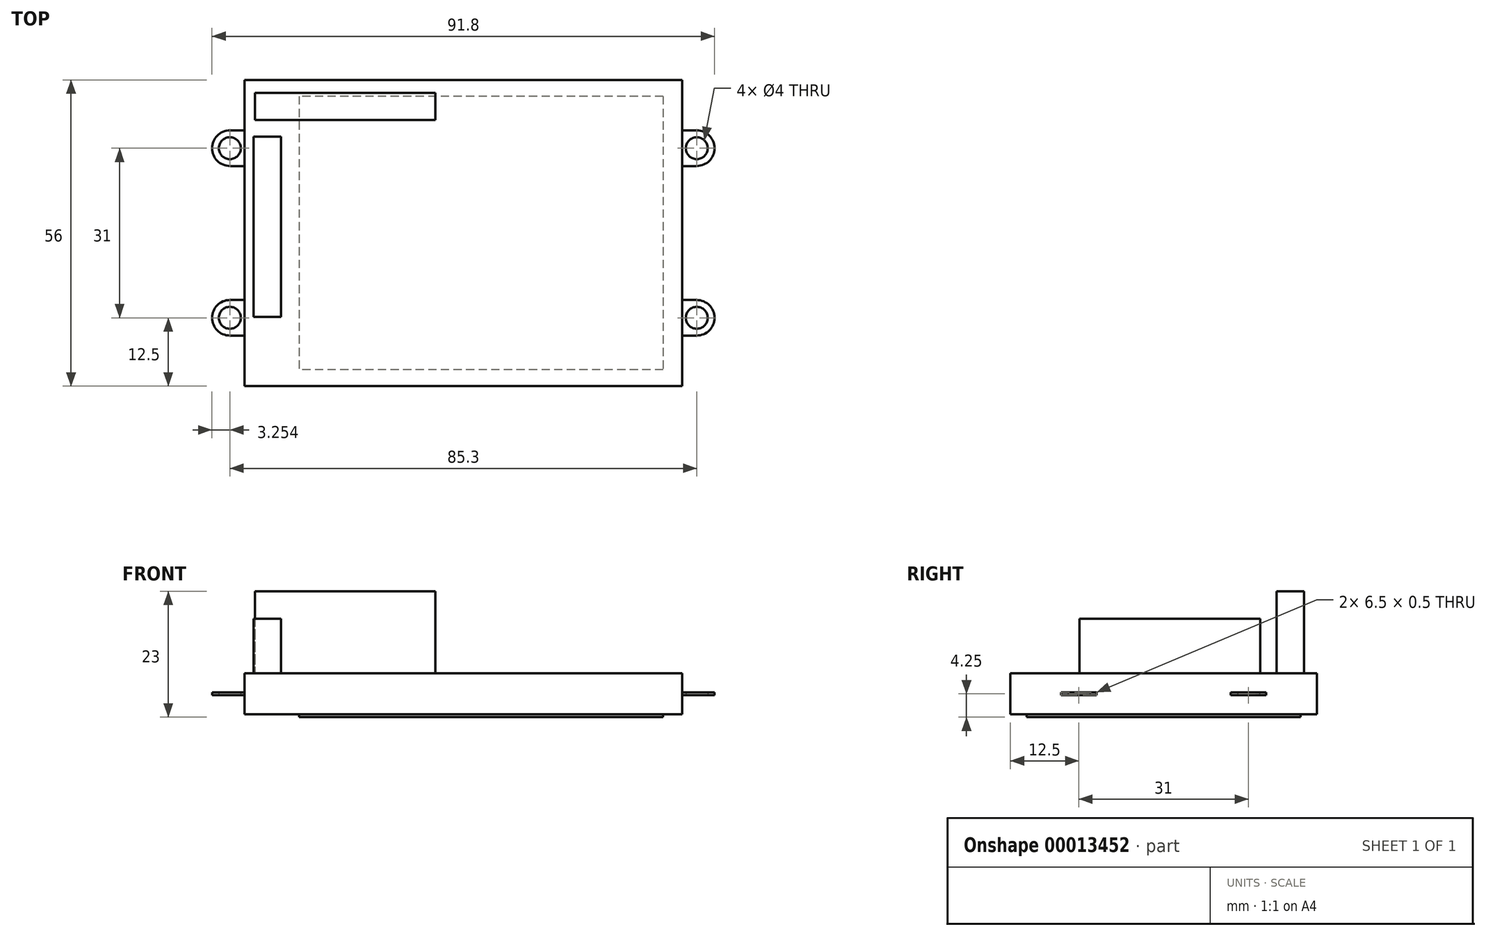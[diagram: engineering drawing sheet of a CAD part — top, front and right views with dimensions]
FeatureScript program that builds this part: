
annotation { "Feature Type Name" : "Feature", "Feature Type Description" : "" }
export const myFeature = defineFeature(function(context is Context, id is Id, definition is map)
    precondition{}
    {
        {
            var Q0;
            Q0=qCreatedBy(makeId("Top.planeOp"),FACE);
            var sketch = newSketch(context, id + "F0", { "sketchPlane" : qUnion([Q0])});
            skLineSegment(sketch, "E0.bottom", {"start": v(-42.56, 23.8) * mm, "end": v(37.44, 23.8) * mm});
            skLineSegment(sketch, "E0.top", {"start": v(-42.56, -32.2) * mm, "end": v(37.44, -32.2) * mm});
            skLineSegment(sketch, "E0.left", {"start": v(-42.56, 23.8) * mm, "end": v(-42.56, -16.44) * mm});
            skLineSegment(sketch, "E0.right", {"start": v(37.44, 23.8) * mm, "end": v(37.44, -32.2) * mm});
            skLineSegment(sketch, "E1", {"start": v(37.44, -22.94) * mm, "end": v(40.1, -22.94) * mm, "construction": true});
            skLineSegment(sketch, "E2", {"start": v(37.44, -16.44) * mm, "end": v(40.1, -16.44) * mm, "construction": true});
            skArc(sketch, "E3", {"start": v(40.1, -22.94) * mm, "mid": v(43.34, -19.7) * mm, "end": v(40.1, -16.44) * mm});
            skCircle(sketch, "E4", {"center": v(40.1, -19.7) * mm, "radius": 2 * mm});
            skLineSegment(sketch, "E5", {"start": v(40.1, -16.44) * mm, "end": v(40.1, -22.94) * mm, "construction": true});
            skLineSegment(sketch, "E6", {"start": v(-2.56, 23.8) * mm, "end": v(-2.56, -32.2) * mm, "construction": true});
            skLineSegment(sketch, "E7", {"start": v(-42.56, -4.2) * mm, "end": v(37.44, -4.2) * mm, "construction": true});
            skLineSegment(sketch, "E8.0.MirrorCS", {"start": v(-45.2, -16.44) * mm, "end": v(-45.2, -22.94) * mm, "construction": true});
            skCircle(sketch, "E8.1.MirrorC", {"center": v(-45.2, -19.7) * mm, "radius": 2 * mm});
            skLineSegment(sketch, "E8.2.MirrorCS", {"start": v(-42.56, -22.94) * mm, "end": v(-45.2, -22.94) * mm, "construction": true});
            skLineSegment(sketch, "E8.3.MirrorCS", {"start": v(-42.56, -16.44) * mm, "end": v(-45.2, -16.44) * mm, "construction": true});
            skArc(sketch, "E8.4.MirrorCS", {"start": v(-45.2, -22.94) * mm, "mid": v(-48.46, -19.7) * mm, "end": v(-45.2, -16.44) * mm});
            skLineSegment(sketch, "E9.3.MirrorCS", {"start": v(37.44, -22.94) * mm, "end": v(40.1, -22.94) * mm});
            skLineSegment(sketch, "E10.1.MirrorCS", {"start": v(-42.56, -16.44) * mm, "end": v(-45.2, -16.44) * mm});
            skLineSegment(sketch, "E10.8.MirrorCS", {"start": v(37.44, -16.44) * mm, "end": v(40.1, -16.44) * mm});
            skLineSegment(sketch, "E11.6.MirrorCS", {"start": v(-42.56, -22.94) * mm, "end": v(-45.2, -22.94) * mm});
            skLineSegment(sketch, "E11.9.MirrorCS", {"start": v(-42.56, 23.8) * mm, "end": v(-42.56, -32.2) * mm});
            skArc(sketch, "E12.0.MirrorCS", {"start": v(-45.2, 14.56) * mm, "mid": v(-48.46, 11.3) * mm, "end": v(-45.2, 8.06) * mm});
            skLineSegment(sketch, "E12.1.MirrorCS", {"start": v(-42.56, 14.56) * mm, "end": v(-45.2, 14.56) * mm, "construction": true});
            skLineSegment(sketch, "E12.2.MirrorCS", {"start": v(-45.2, 8.06) * mm, "end": v(-45.2, 14.56) * mm, "construction": true});
            skLineSegment(sketch, "E12.3.MirrorCS", {"start": v(-42.56, 8.06) * mm, "end": v(-45.2, 8.06) * mm, "construction": true});
            skCircle(sketch, "E12.4.MirrorC", {"center": v(-45.2, 11.3) * mm, "radius": 2 * mm});
            skArc(sketch, "E12.5.MirrorCS", {"start": v(-45.2, 14.56) * mm, "mid": v(-48.46, 11.3) * mm, "end": v(-45.2, 8.06) * mm});
            skLineSegment(sketch, "E12.6.MirrorCS", {"start": v(-45.2, 8.06) * mm, "end": v(-45.2, 14.56) * mm, "construction": true});
            skLineSegment(sketch, "E12.7.MirrorCS", {"start": v(-42.56, 8.06) * mm, "end": v(-45.2, 8.06) * mm});
            skLineSegment(sketch, "E12.8.MirrorCS", {"start": v(-42.56, 14.56) * mm, "end": v(-45.2, 14.56) * mm, "construction": true});
            skCircle(sketch, "E12.9.MirrorC", {"center": v(-45.2, 11.3) * mm, "radius": 2 * mm});
            skLineSegment(sketch, "E12.10.MirrorCS", {"start": v(-42.56, 14.56) * mm, "end": v(-45.2, 14.56) * mm, "construction": true});
            skArc(sketch, "E12.11.MirrorCS", {"start": v(-45.2, 14.56) * mm, "mid": v(-48.46, 11.3) * mm, "end": v(-45.2, 8.06) * mm});
            skLineSegment(sketch, "E12.12.MirrorCS", {"start": v(-45.2, 8.06) * mm, "end": v(-45.2, 14.56) * mm, "construction": true});
            skLineSegment(sketch, "E12.13.MirrorCS", {"start": v(-42.56, 8.06) * mm, "end": v(-45.2, 8.06) * mm, "construction": true});
            skLineSegment(sketch, "E12.14.MirrorCS", {"start": v(-42.56, 14.56) * mm, "end": v(-45.2, 14.56) * mm, "construction": true});
            skCircle(sketch, "E12.15.MirrorC", {"center": v(-45.2, 11.3) * mm, "radius": 2 * mm});
            skArc(sketch, "E12.16.MirrorCS", {"start": v(-45.2, 14.56) * mm, "mid": v(-48.46, 11.3) * mm, "end": v(-45.2, 8.06) * mm});
            skLineSegment(sketch, "E12.17.MirrorCS", {"start": v(-45.2, 8.06) * mm, "end": v(-45.2, 14.56) * mm, "construction": true});
            skLineSegment(sketch, "E12.18.MirrorCS", {"start": v(-42.56, 8.06) * mm, "end": v(-45.2, 8.06) * mm, "construction": true});
            skLineSegment(sketch, "E12.19.MirrorCS", {"start": v(-42.56, 14.56) * mm, "end": v(-45.2, 14.56) * mm, "construction": true});
            skLineSegment(sketch, "E12.20.MirrorCS", {"start": v(-42.56, 8.06) * mm, "end": v(-45.2, 8.06) * mm, "construction": true});
            skCircle(sketch, "E12.21.MirrorC", {"center": v(-45.2, 11.3) * mm, "radius": 2 * mm});
            skArc(sketch, "E12.22.MirrorCS", {"start": v(-45.2, 14.56) * mm, "mid": v(-48.46, 11.3) * mm, "end": v(-45.2, 8.06) * mm});
            skLineSegment(sketch, "E12.23.MirrorCS", {"start": v(-45.2, 8.06) * mm, "end": v(-45.2, 14.56) * mm, "construction": true});
            skLineSegment(sketch, "E12.24.MirrorCS", {"start": v(-42.56, 14.56) * mm, "end": v(-45.2, 14.56) * mm});
            skCircle(sketch, "E12.25.MirrorC", {"center": v(-45.2, 11.3) * mm, "radius": 2 * mm});
            skLineSegment(sketch, "E12.26.MirrorCS", {"start": v(-42.56, 8.06) * mm, "end": v(-45.2, 8.06) * mm, "construction": true});
            skLineSegment(sketch, "E12.27.MirrorCS", {"start": v(-45.2, 8.06) * mm, "end": v(-45.2, 14.56) * mm, "construction": true});
            skCircle(sketch, "E12.28.MirrorC", {"center": v(-45.2, 11.3) * mm, "radius": 2 * mm});
            skArc(sketch, "E12.29.MirrorCS", {"start": v(-45.2, 14.56) * mm, "mid": v(-48.46, 11.3) * mm, "end": v(-45.2, 8.06) * mm});
            skArc(sketch, "E13.0.MirrorCS", {"start": v(40.1, 14.56) * mm, "mid": v(43.34, 11.3) * mm, "end": v(40.1, 8.06) * mm});
            skLineSegment(sketch, "E13.1.MirrorCS", {"start": v(40.1, 8.06) * mm, "end": v(40.1, 14.56) * mm, "construction": true});
            skLineSegment(sketch, "E13.2.MirrorCS", {"start": v(37.44, 14.56) * mm, "end": v(40.1, 14.56) * mm, "construction": true});
            skLineSegment(sketch, "E13.3.MirrorCS", {"start": v(37.44, 8.06) * mm, "end": v(40.1, 8.06) * mm, "construction": true});
            skArc(sketch, "E13.4.MirrorCS", {"start": v(40.1, 14.56) * mm, "mid": v(43.34, 11.3) * mm, "end": v(40.1, 8.06) * mm});
            skLineSegment(sketch, "E13.5.MirrorCS", {"start": v(37.44, 14.56) * mm, "end": v(40.1, 14.56) * mm});
            skLineSegment(sketch, "E13.6.MirrorCS", {"start": v(37.44, 8.06) * mm, "end": v(40.1, 8.06) * mm, "construction": true});
            skLineSegment(sketch, "E13.7.MirrorCS", {"start": v(40.1, 8.06) * mm, "end": v(40.1, 14.56) * mm, "construction": true});
            skCircle(sketch, "E13.8.MirrorC", {"center": v(40.1, 11.3) * mm, "radius": 2 * mm});
            skLineSegment(sketch, "E13.9.MirrorCS", {"start": v(37.44, 8.06) * mm, "end": v(40.1, 8.06) * mm});
            skCircle(sketch, "E13.10.MirrorC", {"center": v(40.1, 11.3) * mm, "radius": 2 * mm});
            skArc(sketch, "E13.11.MirrorCS", {"start": v(40.1, 14.56) * mm, "mid": v(43.34, 11.3) * mm, "end": v(40.1, 8.06) * mm});
            skLineSegment(sketch, "E13.12.MirrorCS", {"start": v(37.44, 14.56) * mm, "end": v(40.1, 14.56) * mm, "construction": true});
            skLineSegment(sketch, "E13.13.MirrorCS", {"start": v(40.1, 8.06) * mm, "end": v(40.1, 14.56) * mm, "construction": true});
            skCircle(sketch, "E13.14.MirrorC", {"center": v(40.1, 11.3) * mm, "radius": 2 * mm});
            skLineSegment(sketch, "E14", {"start": v(-42.56, -16.44) * mm, "end": v(-42.56, -22.94) * mm});
            skLineSegment(sketch, "E15.trimOffspring", {"start": v(-42.56, -22.94) * mm, "end": v(-42.56, -32.2) * mm});
            skSolve(sketch);
        }
        {
            var Q0;
            Q0=makeQuery(id+"F0.imprint","IMPRINT",FACE,{"disambiguationData":[TD([[makeQuery(id+"F0.imprint","IMPRINT",EDGE,{"derivedFrom":sQuery(id+"F0.wireOp",EDGE,"E0.bottom")}),-1.0]])]});
            extrude(context, id + "F1", {"entities" : qUnion([Q0]), "endBound" : BoundingType.SYMMETRIC, "oppositeDirection" : true, "depth" : 7.5 * mm});
        }
        {
            var Q0;
            Q0=makeQuery(id+"F0.imprint","IMPRINT",FACE,{"disambiguationData":[TD([[makeQuery(id+"F0.imprint","IMPRINT",EDGE,{"derivedFrom":sQuery(id+"F0.wireOp",EDGE,"E10.1.MirrorCS")}),1.0]])]});
            var Q1;
            {var subQ2=sQuery(id+"F0.wireOp",EDGE,"E9.3.MirrorCS");Q1=makeQuery(id+"F0.imprint","IMPRINT",FACE,{"disambiguationData":[TD([[makeQuery(id+"F0.imprint","IMPRINT",EDGE,{"derivedFrom":subQ2}),1.0]])]});}
            var Q2;
            {var subQ1=sQuery(id+"F0.wireOp",EDGE,"E12.7.MirrorCS");Q2=makeQuery(id+"F0.imprint","IMPRINT",FACE,{"disambiguationData":[TD([[makeQuery(id+"F0.imprint","IMPRINT",EDGE,{"derivedFrom":subQ1}),-1.0]])]});}
            var Q3;
            {var subQ1=sQuery(id+"F0.wireOp",EDGE,"E13.5.MirrorCS");Q3=makeQuery(id+"F0.imprint","IMPRINT",FACE,{"disambiguationData":[TD([[makeQuery(id+"F0.imprint","IMPRINT",EDGE,{"derivedFrom":subQ1}),-1.0]])]});}
            extrude(context, id + "F2", {"entities" : qUnion([Q0, Q1, Q2, Q3]), "operationType" : NewBodyOperationType.ADD, "endBound" : BoundingType.SYMMETRIC, "depth" : 0.5 * mm});
        }
        {
            var Q0;
            Q0=makeQuery(id+"F1.opExtrude","CAP_FACE",FACE,{"disambiguationData":[OSD([sQuery(id+"F0.wireOp",EDGE,"E0.bottom"),sQuery(id+"F0.wireOp",EDGE,"E0.top"),sQuery(id+"F0.wireOp",EDGE,"E0.right"),sQuery(id+"F0.wireOp",EDGE,"E0.left"),sQuery(id+"F0.wireOp",EDGE,"E14"),sQuery(id+"F0.wireOp",EDGE,"E15.trimOffspring")])],"isStart":false});
            var sketch = newSketch(context, id + "F3", { "sketchPlane" : qUnion([Q0])});
            skLineSegment(sketch, "E16.bottom", {"start": v(33.94, -20.8) * mm, "end": v(-32.56, -20.8) * mm});
            skLineSegment(sketch, "E16.top", {"start": v(33.94, 29.2) * mm, "end": v(-32.56, 29.2) * mm});
            skLineSegment(sketch, "E16.left", {"start": v(33.94, -20.8) * mm, "end": v(33.94, 29.2) * mm});
            skLineSegment(sketch, "E16.right", {"start": v(-32.56, -20.8) * mm, "end": v(-32.56, 29.2) * mm});
            skLineSegment(sketch, "E17", {"start": v(-12.4, -23.8) * mm, "end": v(-12.4, -20.8) * mm, "construction": true});
            skLineSegment(sketch, "E18", {"start": v(-12.54, 29.2) * mm, "end": v(-12.54, 32.2) * mm, "construction": true});
            skSolve(sketch);
        }
        {
            var Q0;
            Q0=makeQuery(id+"F3.imprint","IMPRINT",FACE,{"disambiguationData":[TD([[makeQuery(id+"F3.imprint","IMPRINT",EDGE,{"derivedFrom":sQuery(id+"F3.wireOp",EDGE,"E16.bottom")}),-1.0]])]});
            extrude(context, id + "F4", {"entities" : qUnion([Q0]), "operationType" : NewBodyOperationType.ADD, "depth" : 0.5 * mm});
        }
        {
            var Q0;
            Q0=makeQuery(id+"F1.opExtrude","CAP_FACE",FACE,{"disambiguationData":[OSD([sQuery(id+"F0.wireOp",EDGE,"E0.bottom"),sQuery(id+"F0.wireOp",EDGE,"E0.top"),sQuery(id+"F0.wireOp",EDGE,"E0.right"),sQuery(id+"F0.wireOp",EDGE,"E0.left"),sQuery(id+"F0.wireOp",EDGE,"E14"),sQuery(id+"F0.wireOp",EDGE,"E15.trimOffspring")])],"isStart":true});
            var sketch = newSketch(context, id + "F5", { "sketchPlane" : qUnion([Q0])});
            skLineSegment(sketch, "E19.bottom", {"start": v(-40.63, 21.45) * mm, "end": v(-7.63, 21.45) * mm});
            skLineSegment(sketch, "E19.top", {"start": v(-40.63, 16.45) * mm, "end": v(-7.63, 16.45) * mm});
            skLineSegment(sketch, "E19.left", {"start": v(-40.63, 21.45) * mm, "end": v(-40.63, 16.45) * mm});
            skLineSegment(sketch, "E19.right", {"start": v(-7.63, 21.45) * mm, "end": v(-7.63, 16.45) * mm});
            skSolve(sketch);
        }
        {
            var Q0;
            Q0=qSketchRegion(id+"F5",true);
            extrude(context, id + "F6", {"entities" : qUnion([Q0]), "operationType" : NewBodyOperationType.ADD, "depth" : 15 * mm});
        }
        {
            var Q0;
            Q0=makeQuery(id+"F1.opExtrude","CAP_FACE",FACE,{"disambiguationData":[OSD([sQuery(id+"F0.wireOp",EDGE,"E0.bottom"),sQuery(id+"F0.wireOp",EDGE,"E0.top"),sQuery(id+"F0.wireOp",EDGE,"E0.right"),sQuery(id+"F0.wireOp",EDGE,"E0.left"),sQuery(id+"F0.wireOp",EDGE,"E14"),sQuery(id+"F0.wireOp",EDGE,"E15.trimOffspring")])],"isStart":true});
            var sketch = newSketch(context, id + "F7", { "sketchPlane" : qUnion([Q0])});
            skLineSegment(sketch, "E20.left", {"start": v(-40.88, -19.55) * mm, "end": v(-40.88, 13.45) * mm});
            skLineSegment(sketch, "E20.bottom", {"start": v(-40.88, -19.55) * mm, "end": v(-35.88, -19.55) * mm});
            skLineSegment(sketch, "E20.top", {"start": v(-40.88, 13.45) * mm, "end": v(-35.88, 13.45) * mm});
            skLineSegment(sketch, "E20.right", {"start": v(-35.88, -19.55) * mm, "end": v(-35.88, 13.45) * mm});
            skSolve(sketch);
        }
        {
            var Q0;
            Q0=qSketchRegion(id+"F7",true);
            extrude(context, id + "F8", {"entities" : qUnion([Q0]), "operationType" : NewBodyOperationType.ADD, "depth" : 10 * mm});
        }
    });
